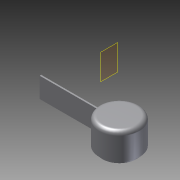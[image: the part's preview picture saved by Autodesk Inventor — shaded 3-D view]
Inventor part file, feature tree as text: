
AUTODESK INVENTOR PART (.ipt)
format: ipt  version: 2012 (Build 160160000, 160)  size: 105,984 bytes
history: native  units: in
note: dims shown in document units (in); Inventor stores cm internally (conversion verified against a paired STEP export)
features: extrude x3, sketch x3, fillet x1, plane x1
ambient origin geometry x8: Origin, YZ Plane, XZ Plane, XY Plane, X Axis, Y Axis, Z Axis, Center Point
bodies: Solid1 (feature_tree)
feature tree (8):
  extrude  "Extrusion1"  Depth=1.0281in TaperAngle=0.0deg
  extrude  "Extrusion2"  Depth=0.1314in TaperAngle=0.0deg
  fillet  "Fillet1"  Radius=0.1575in
  plane  "Work Plane1"
  extrude  "Extrusion3"  Depth=0.0295in
  sketch  "Sketch2"  dims[d0=1.5748in d1=1.0281in d2=0.0in]
  sketch  "Sketch3"  dims[d3=0.1181in d4=0.1314in d5=0.0in d6=0.1575in]
  sketch  "Sketch4"  dims[d7=0.7874in d8=0.0295in d9=0.0295in d10=0.0394in d11=0.9936in d12=2.2968in d13=0.0in d14=0.0in]
